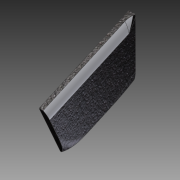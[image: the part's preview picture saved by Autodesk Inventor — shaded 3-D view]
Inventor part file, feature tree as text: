
AUTODESK INVENTOR PART (.ipt)
format: ipt  version: 2012 (Build 160160000, 160)  size: 411,136 bytes
history: native  units: mm
features: fillet x15, extrude x11, sketch x2, chamfer x1
ambient origin geometry x8: Origin, YZ Plane, XZ Plane, XY Plane, X Axis, Y Axis, Z Axis, Center Point
feature tree (29):
  sketch  "Sketch2"  dims[d14=52.0mm d15=23.0mm d16=22.6mm d17=8.2mm d18=11.5mm d19=11.5mm d20=10.2mm d21=10.2mm d22=8.0mm d23=20.0mm d25=30.0mm d26=0.0mm d27=11.8mm d28=0.0mm]
  extrude  "Extrusion3"  Depth=11.8mm TaperAngle=0.0deg
  extrude  "Extrusion4"  Depth=1.5mm
  fillet  "Fillet1"  Radius=4.18879mm
  fillet  "Fillet2"  Radius=70.0mm
  extrude  "Extrusion5"  Depth=3.0mm
  extrude  "Extrusion6"  Depth=34.0mm
  extrude  "Extrusion7"  Depth=30.0mm TaperAngle=0.0deg
  fillet  "Fillet3"  Radius=24.0mm
  fillet  "Fillet4"  Radius=28.0mm
  fillet  "Fillet5"  Radius=18.0mm
  fillet  "Fillet6"  Radius=28.0mm
  fillet  "Fillet7"  Radius=22.0mm
  chamfer  "Chamfer1"  Distance=24.0mm
  fillet  "Fillet8"  Radius=117.0mm
  fillet  "Fillet9"  Radius=54.0mm
  fillet  "Fillet10"  Radius=43.0mm
  fillet  "Fillet11"  Radius=12.0mm
  fillet  "Fillet12"  Radius=15.0mm
  extrude  "Extrusion8"  Depth=10.0mm
  fillet  "Fillet13"  Radius=4.0mm
  fillet  "Fillet14"  Radius=10.0mm
  sketch  "Sketch3"  dims[d29=4.5mm d30=1.5mm d37=4.18879mm d38=70.0mm d39=3.0mm d40=34.0mm d41=30.0mm d42=0.0mm d43=24.0mm d44=0.0mm d45=28.0mm d46=18.0mm d47=28.0mm d48=22.0mm d49=24.0mm d50=0.0mm d52=117.0mm d53=54.0mm d54=43.0mm d55=12.0mm d56=15.0mm d57=10.0mm d58=4.0mm d59=10.0mm d60=5.0mm d61=2.0mm d62=45.0deg d63=20.0mm d64=2.0mm d65=108.0mm d66=2.0mm d67=20.0mm d68=4.5mm d69=5.8mm d70=24.4mm d71=0.0mm d72=5.0mm d73=1.5mm d74=38.0mm d75=90.0mm d76=12.6mm d77=0.0mm d78=11.0mm d79=19.0mm d80=42.0mm d81=7.0mm d82=0.0mm d83=2.0mm d84=4.0mm d85=66.0mm d86=6.0mm d88=60.0mm d89=8.0mm d90=3.0mm d91=3.0mm d92=3.0mm d93=3.0mm d94=3.0mm d95=3.0mm d96=3.0mm d97=3.0mm d98=10.0mm d99=40.0mm d100=0.0mm d101=0.0mm d102=11.0mm d103=10.0mm d104=0.0mm d105=0.0mm d106=10.9mm d107=0.0mm d108=38.0mm]
  extrude  "Extrusion9"  Depth=5.0mm TaperAngle=45.0deg
  extrude  "Extrusion10"  Depth=20.0mm
  fillet  "Fillet15"  Radius=2.0mm
  extrude  "Extrusion11"  Depth=108.0mm
  extrude  "Extrusion12"  Depth=2.0mm
  extrude  "Extrusion13"  Depth=20.0mm
